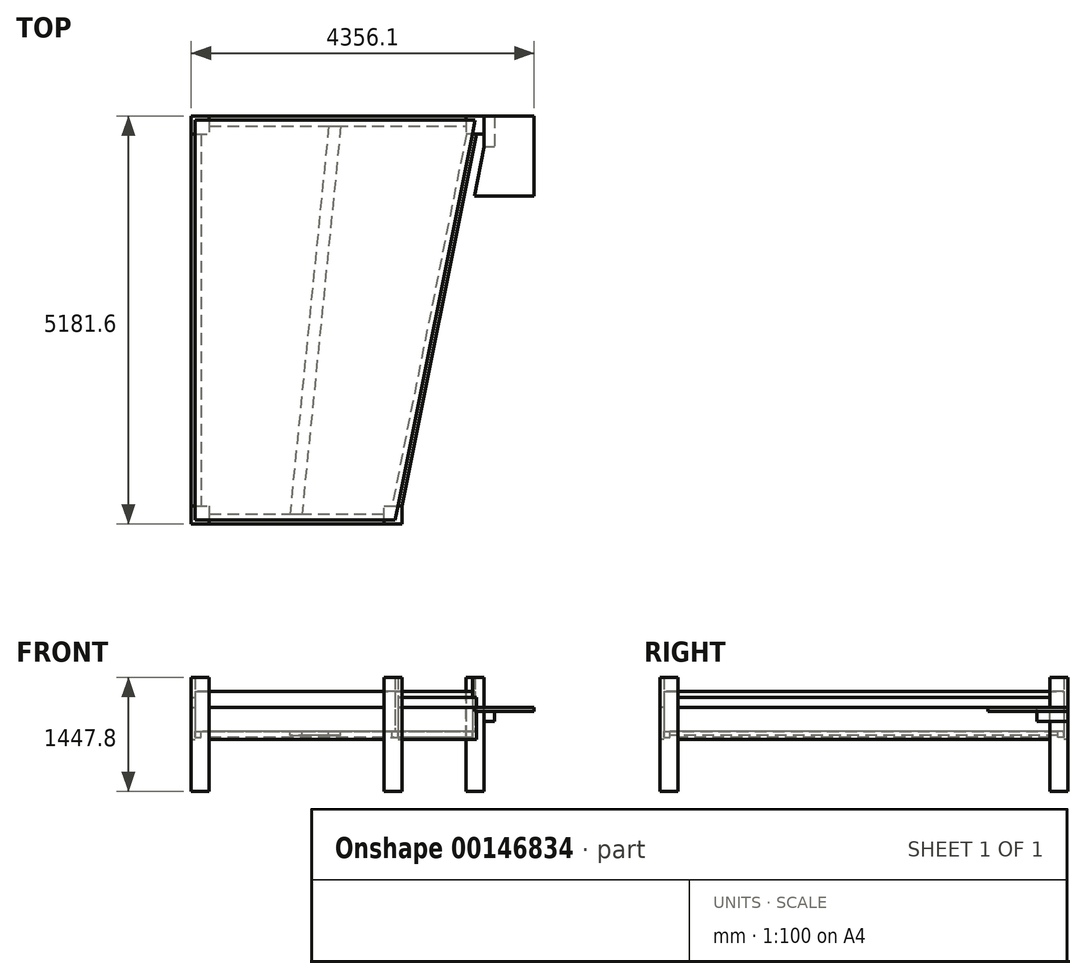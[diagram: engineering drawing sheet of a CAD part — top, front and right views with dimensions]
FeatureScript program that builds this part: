
annotation { "Feature Type Name" : "Feature", "Feature Type Description" : "" }
export const myFeature = defineFeature(function(context is Context, id is Id, definition is map)
    precondition{}
    {
        {
            var Q0;
            Q0=qCreatedBy(makeId("Top.planeOp"),FACE);
            var sketch = newSketch(context, id + "F0", { "sketchPlane" : qUnion([Q0])});
            skLineSegment(sketch, "E0", {"start": v(0, 0) * mm, "end": v(0, 5080) * mm});
            skLineSegment(sketch, "E1", {"start": v(0, 5080) * mm, "end": v(3556, 5080) * mm});
            skLineSegment(sketch, "E2", {"start": v(3556, 5080) * mm, "end": v(2540, 0) * mm});
            skPoint(sketch, "E2.endSnap0", {"position": v(1778, 5080) * mm});
            skLineSegment(sketch, "E3", {"start": v(2540, 0) * mm, "end": v(0, 0) * mm});
            skLineSegment(sketch, "E4.bottom", {"start": v(-50.8, 5130.8) * mm, "end": v(177.8, 5130.8) * mm});
            skLineSegment(sketch, "E4.top", {"start": v(-50.8, 4902.2) * mm, "end": v(177.8, 4902.2) * mm});
            skLineSegment(sketch, "E4.left", {"start": v(-50.8, 5130.8) * mm, "end": v(-50.8, 4902.2) * mm});
            skLineSegment(sketch, "E4.right", {"start": v(177.8, 5130.8) * mm, "end": v(177.8, 4902.2) * mm});
            skPoint(sketch, "E4.middle", {"position": v(0, 5080) * mm});
            skLineSegment(sketch, "E5.bottom", {"start": v(3670.3, 5130.8) * mm, "end": v(3441.7, 5130.8) * mm});
            skLineSegment(sketch, "E5.top", {"start": v(3670.3, 4902.2) * mm, "end": v(3441.7, 4902.2) * mm});
            skLineSegment(sketch, "E5.left", {"start": v(3670.3, 5130.8) * mm, "end": v(3670.3, 4902.2) * mm});
            skLineSegment(sketch, "E5.right", {"start": v(3441.7, 5130.8) * mm, "end": v(3441.7, 4902.2) * mm});
            skPoint(sketch, "E5.middle", {"position": v(3556, 5080) * mm});
            skLineSegment(sketch, "E6", {"start": v(177.8, 5130.8) * mm, "end": v(3441.7, 5130.8) * mm});
            skLineSegment(sketch, "E7.bottom", {"start": v(2398.77, -50.8) * mm, "end": v(2627.37, -50.8) * mm});
            skLineSegment(sketch, "E7.top", {"start": v(2398.77, 177.8) * mm, "end": v(2627.37, 177.8) * mm});
            skLineSegment(sketch, "E7.left", {"start": v(2398.77, -50.8) * mm, "end": v(2398.77, 177.8) * mm});
            skLineSegment(sketch, "E7.right", {"start": v(2627.37, -50.8) * mm, "end": v(2627.37, 177.8) * mm});
            skLineSegment(sketch, "E8", {"start": v(2627.37, 177.8) * mm, "end": v(3572.25, 4902.2) * mm});
            skLineSegment(sketch, "E9.bottom", {"start": v(-50.8, 177.8) * mm, "end": v(177.8, 177.8) * mm});
            skLineSegment(sketch, "E9.top", {"start": v(-50.8, -50.8) * mm, "end": v(177.8, -50.8) * mm});
            skLineSegment(sketch, "E9.left", {"start": v(-50.8, 177.8) * mm, "end": v(-50.8, -50.8) * mm});
            skLineSegment(sketch, "E9.right", {"start": v(177.8, 177.8) * mm, "end": v(177.8, -50.8) * mm});
            skLineSegment(sketch, "E10", {"start": v(177.8, -50.8) * mm, "end": v(2398.77, -50.8) * mm});
            skLineSegment(sketch, "E11", {"start": v(-50.8, 4902.2) * mm, "end": v(-50.8, 177.8) * mm});
            skLineSegment(sketch, "E12", {"start": v(76.2, 4902.2) * mm, "end": v(76.2, 177.8) * mm});
            skLineSegment(sketch, "E13", {"start": v(177.8, 76.2) * mm, "end": v(2398.77, 76.2) * mm});
            skLineSegment(sketch, "E14", {"start": v(177.8, 5003.8) * mm, "end": v(3441.7, 5003.8) * mm});
            skLineSegment(sketch, "E15", {"start": v(3442.73, 4902.2) * mm, "end": v(2497.85, 177.8) * mm});
            skLineSegment(sketch, "E16", {"start": v(1270, 0) * mm, "end": v(1778, 5080) * mm, "construction": true});
            skLineSegment(sketch, "E17", {"start": v(1854.58, 5080) * mm, "end": v(1346.58, 0) * mm});
            skLineSegment(sketch, "E18.MirrorCS", {"start": v(1701.42, 5080) * mm, "end": v(1193.42, 0) * mm});
            skSolve(sketch);
        }
        {
            var Q0;
            {var subQ6=sQuery(id+"F0.wireOp",EDGE,"E7.bottom");Q0=makeQuery(id+"F0.imprint","IMPRINT",FACE,{"disambiguationData":[TD([[makeQuery(id+"F0.imprint","IMPRINT",EDGE,{"derivedFrom":subQ6}),1.0]])]});}
            var Q1;
            {var subQ0=sQuery(id+"F0.wireOp",EDGE,"E3");var subQ1=sQuery(id+"F0.wireOp",EDGE,"E2");var subQ2=makeQuery(id+"F0.imprint","INTERSECT",VERTEX,{"derivedFrom":[subQ1,subQ0]});Q1=makeQuery(id+"F0.imprint","IMPRINT",FACE,{"disambiguationData":[TD([[makeQuery(id+"F0.imprint","IMPRINT",EDGE,{"disambiguationData":[TD([[subQ2,1.0]])],"derivedFrom":subQ1}),-1.0]])]});}
            var Q2;
            {var subQ0=sQuery(id+"F0.wireOp",EDGE,"E5.bottom");Q2=makeQuery(id+"F0.imprint","IMPRINT",FACE,{"disambiguationData":[TD([[makeQuery(id+"F0.imprint","IMPRINT",EDGE,{"derivedFrom":subQ0}),1.0]])]});}
            var Q3;
            {var subQ0=sQuery(id+"F0.wireOp",EDGE,"E2");var subQ1=sQuery(id+"F0.wireOp",EDGE,"E1");var subQ2=makeQuery(id+"F0.imprint","INTERSECT",VERTEX,{"derivedFrom":[subQ1,subQ0]});Q3=makeQuery(id+"F0.imprint","IMPRINT",FACE,{"disambiguationData":[TD([[makeQuery(id+"F0.imprint","IMPRINT",EDGE,{"disambiguationData":[TD([[subQ2,1.0]])],"derivedFrom":subQ1}),-1.0]])]});}
            var Q4;
            {var subQ0=sQuery(id+"F0.wireOp",EDGE,"E9.top");Q4=makeQuery(id+"F0.imprint","IMPRINT",FACE,{"disambiguationData":[TD([[makeQuery(id+"F0.imprint","IMPRINT",EDGE,{"derivedFrom":subQ0}),1.0]])]});}
            var Q5;
            {var subQ0=sQuery(id+"F0.wireOp",EDGE,"E3");var subQ1=sQuery(id+"F0.wireOp",EDGE,"E0");var subQ2=makeQuery(id+"F0.imprint","INTERSECT",VERTEX,{"derivedFrom":[subQ1,subQ0]});Q5=makeQuery(id+"F0.imprint","IMPRINT",FACE,{"disambiguationData":[TD([[makeQuery(id+"F0.imprint","IMPRINT",EDGE,{"disambiguationData":[TD([[subQ2,-1.0]])],"derivedFrom":subQ1}),-1.0]])]});}
            var Q6;
            {var subQ0=sQuery(id+"F0.wireOp",EDGE,"E1");var subQ1=sQuery(id+"F0.wireOp",EDGE,"E0");var subQ2=makeQuery(id+"F0.imprint","INTERSECT",VERTEX,{"derivedFrom":[subQ1,subQ0]});Q6=makeQuery(id+"F0.imprint","IMPRINT",FACE,{"disambiguationData":[TD([[makeQuery(id+"F0.imprint","IMPRINT",EDGE,{"disambiguationData":[TD([[subQ2,1.0]])],"derivedFrom":subQ1}),-1.0]])]});}
            var Q7;
            {var subQ4=sQuery(id+"F0.wireOp",EDGE,"E4.bottom");Q7=makeQuery(id+"F0.imprint","IMPRINT",FACE,{"disambiguationData":[TD([[makeQuery(id+"F0.imprint","IMPRINT",EDGE,{"derivedFrom":subQ4}),-1.0]])]});}
            extrude(context, id + "F1", {"entities" : qUnion([Q0, Q1, Q2, Q3, Q4, Q5, Q6, Q7]), "oppositeDirection" : true, "depth" : 762 * mm});
        }
        {
            var Q0;
            {var subQ0=sQuery(id+"F0.wireOp",EDGE,"E9.top");Q0=makeQuery(id+"F0.imprint","IMPRINT",FACE,{"disambiguationData":[TD([[makeQuery(id+"F0.imprint","IMPRINT",EDGE,{"derivedFrom":subQ0}),1.0]])]});}
            var Q1;
            {var subQ6=sQuery(id+"F0.wireOp",EDGE,"E7.bottom");Q1=makeQuery(id+"F0.imprint","IMPRINT",FACE,{"disambiguationData":[TD([[makeQuery(id+"F0.imprint","IMPRINT",EDGE,{"derivedFrom":subQ6}),1.0]])]});}
            var Q2;
            {var subQ0=sQuery(id+"F0.wireOp",EDGE,"E5.bottom");Q2=makeQuery(id+"F0.imprint","IMPRINT",FACE,{"disambiguationData":[TD([[makeQuery(id+"F0.imprint","IMPRINT",EDGE,{"derivedFrom":subQ0}),1.0]])]});}
            var Q3;
            {var subQ4=sQuery(id+"F0.wireOp",EDGE,"E4.bottom");Q3=makeQuery(id+"F0.imprint","IMPRINT",FACE,{"disambiguationData":[TD([[makeQuery(id+"F0.imprint","IMPRINT",EDGE,{"derivedFrom":subQ4}),-1.0]])]});}
            extrude(context, id + "F2", {"entities" : qUnion([Q0, Q1, Q2, Q3]), "operationType" : NewBodyOperationType.ADD, "depth" : 685.8 * mm});
        }
        {
            var Q0;
            {var subQ5=sQuery(id+"F0.wireOp",EDGE,"E11");Q0=makeQuery(id+"F0.imprint","IMPRINT",FACE,{"disambiguationData":[TD([[makeQuery(id+"F0.imprint","IMPRINT",EDGE,{"derivedFrom":subQ5}),1.0]])]});}
            var Q1;
            {var subQ5=sQuery(id+"F0.wireOp",EDGE,"E6");Q1=makeQuery(id+"F0.imprint","IMPRINT",FACE,{"disambiguationData":[TD([[makeQuery(id+"F0.imprint","IMPRINT",EDGE,{"derivedFrom":subQ5}),-1.0]])]});}
            var Q2;
            {var subQ4=sQuery(id+"F0.wireOp",EDGE,"E2");var subQ6=sQuery(id+"F0.wireOp",EDGE,"E5.top");var subQ8=makeQuery(id+"F0.imprint","INTERSECT",VERTEX,{"derivedFrom":[subQ4,subQ6]});Q2=makeQuery(id+"F0.imprint","IMPRINT",FACE,{"disambiguationData":[TD([[makeQuery(id+"F0.imprint","IMPRINT",EDGE,{"disambiguationData":[TD([[subQ8,-1.0]])],"derivedFrom":subQ4}),1.0]])]});}
            var Q3;
            {var subQ5=sQuery(id+"F0.wireOp",EDGE,"E10");Q3=makeQuery(id+"F0.imprint","IMPRINT",FACE,{"disambiguationData":[TD([[makeQuery(id+"F0.imprint","IMPRINT",EDGE,{"derivedFrom":subQ5}),1.0]])]});}
            extrude(context, id + "F3", {"entities" : qUnion([Q0, Q1, Q2, Q3]), "depth" : 304.8 * mm, "hasSecondDirection" : true, "secondDirectionOppositeDirection" : true, "secondDirectionDepth" : 101.6 * mm});
        }
        {
            var Q0;
            Q0=makeQuery(id+"F3.opExtrude","CAP_FACE",FACE,{"disambiguationData":[OSD([sQuery(id+"F0.wireOp",EDGE,"E2"),sQuery(id+"F0.wireOp",EDGE,"E5.top"),sQuery(id+"F0.wireOp",EDGE,"E7.top"),sQuery(id+"F0.wireOp",EDGE,"E8")])],"isStart":false});
            var sketch = newSketch(context, id + "F4", { "sketchPlane" : qUnion([Q0])});
            skLineSegment(sketch, "E19.0", {"start": v(3670.3, 4902.2) * mm, "end": v(3441.7, 4902.2) * mm});
            skLineSegment(sketch, "E19.1", {"start": v(3556, 5080) * mm, "end": v(2540, 0) * mm});
            skLineSegment(sketch, "E19.2", {"start": v(3670.3, 5130.8) * mm, "end": v(3441.7, 5130.8) * mm});
            skLineSegment(sketch, "E19.3", {"start": v(3441.7, 5130.8) * mm, "end": v(3441.7, 4902.2) * mm});
            skLineSegment(sketch, "E19.4", {"start": v(177.8, 5130.8) * mm, "end": v(3441.7, 5130.8) * mm});
            skLineSegment(sketch, "E19.6", {"start": v(3670.3, 5130.8) * mm, "end": v(3670.3, 4902.2) * mm});
            skLineSegment(sketch, "E19.7", {"start": v(0, 5080) * mm, "end": v(3556, 5080) * mm});
            skLineSegment(sketch, "E19.8", {"start": v(3670.3, 5130.8) * mm, "end": v(4305.3, 5130.8) * mm});
            skLineSegment(sketch, "E19.9", {"start": v(2627.37, 177.8) * mm, "end": v(3572.25, 4902.2) * mm});
            skLineSegment(sketch, "E19.11", {"start": v(3616.97, 4902.2) * mm, "end": v(3441.7, 4902.2) * mm});
            skLineSegment(sketch, "E19.12", {"start": v(3670.3, 5130.8) * mm, "end": v(3441.7, 5130.8) * mm});
            skLineSegment(sketch, "E19.13", {"start": v(3441.7, 5080) * mm, "end": v(3441.7, 4902.2) * mm});
            skLineSegment(sketch, "E19.14", {"start": v(3670.3, 5130.8) * mm, "end": v(3670.3, 4902.2) * mm});
            skLineSegment(sketch, "E19.15", {"start": v(3556, 5080) * mm, "end": v(3520.44, 4902.2) * mm});
            skLineSegment(sketch, "E19.16", {"start": v(3520.44, 4902.2) * mm, "end": v(2575.56, 177.8) * mm});
            skLineSegment(sketch, "E19.17", {"start": v(177.8, 5080) * mm, "end": v(3441.7, 5080) * mm});
            skLineSegment(sketch, "E19.18", {"start": v(177.8, 5130.8) * mm, "end": v(3441.7, 5130.8) * mm});
            skLineSegment(sketch, "E19.19", {"start": v(3441.7, 5130.8) * mm, "end": v(3441.7, 5080) * mm});
            skLineSegment(sketch, "E19.20", {"start": v(3670.3, 4902.2) * mm, "end": v(3441.7, 4902.2) * mm});
            skLineSegment(sketch, "E19.21", {"start": v(3441.7, 5130.8) * mm, "end": v(3441.7, 4902.2) * mm});
            skLineSegment(sketch, "E19.22", {"start": v(3441.7, 5080) * mm, "end": v(3556, 5080) * mm});
            skLineSegment(sketch, "E19.25", {"start": v(3670.3, 4902.2) * mm, "end": v(3520.44, 4902.2) * mm});
            skLineSegment(sketch, "E19.26", {"start": v(2627.37, 177.8) * mm, "end": v(3572.25, 4902.2) * mm});
            skLineSegment(sketch, "E19.27", {"start": v(3520.44, 4902.2) * mm, "end": v(2575.56, 177.8) * mm});
            skLineSegment(sketch, "E19.28", {"start": v(177.8, 5130.8) * mm, "end": v(3441.7, 5130.8) * mm});
            skLineSegment(sketch, "E19.29", {"start": v(177.8, 5080) * mm, "end": v(3441.7, 5080) * mm});
            skLineSegment(sketch, "E19.35", {"start": v(3670.3, 5130.8) * mm, "end": v(3441.7, 5130.8) * mm});
            skLineSegment(sketch, "E19.38", {"start": v(3670.3, 5130.8) * mm, "end": v(3670.3, 4902.2) * mm});
            skLineSegment(sketch, "E19.39", {"start": v(2627.37, 177.8) * mm, "end": v(3572.25, 4902.2) * mm});
            skLineSegment(sketch, "E19.42", {"start": v(3441.7, 5130.8) * mm, "end": v(3441.7, 5080) * mm});
            skLineSegment(sketch, "E19.45", {"start": v(3572.25, 4902.2) * mm, "end": v(3520.44, 4902.2) * mm});
            skLineSegment(sketch, "E19.46", {"start": v(3441.7, 5130.8) * mm, "end": v(3441.7, 5080) * mm});
            skLineSegment(sketch, "E19.47", {"start": v(3572.25, 4902.2) * mm, "end": v(3520.44, 4902.2) * mm});
            skLineSegment(sketch, "E20", {"start": v(4305.3, 5130.8) * mm, "end": v(4305.3, 4114.8) * mm});
            skLineSegment(sketch, "E21", {"start": v(4305.3, 4114.8) * mm, "end": v(3414.77, 4114.8) * mm});
            skLineSegment(sketch, "E22", {"start": v(3799.33, 5130.8) * mm, "end": v(3799.33, 4734.53) * mm});
            skLineSegment(sketch, "E23", {"start": v(3799.33, 4734.53) * mm, "end": v(3670.3, 4734.53) * mm});
            skLineSegment(sketch, "E24", {"start": v(3670.3, 4734.53) * mm, "end": v(3546.35, 4114.8) * mm});
            skLineSegment(sketch, "E25", {"start": v(3670.3, 4902.2) * mm, "end": v(3670.3, 4734.53) * mm});
            skSolve(sketch);
        }
        {
            var Q0;
            Q0=makeQuery(id+"F4.imprint","IMPRINT",FACE,{"disambiguationData":[TD([[makeQuery(id+"F4.imprint","IMPRINT",EDGE,{"derivedFrom":sQuery(id+"F4.wireOp",EDGE,"E19.8")}),-1.0]])]});
            var Q1;
            {var subQ2=sQuery(id+"F4.wireOp",EDGE,"E19.25");Q1=makeQuery(id+"F4.imprint","IMPRINT",FACE,{"disambiguationData":[TD([[makeQuery(id+"F4.imprint","IMPRINT",EDGE,{"derivedFrom":subQ2}),1.0]])]});}
            extrude(context, id + "F5", {"entities" : qUnion([Q0, Q1]), "oppositeDirection" : true, "depth" : 179.83 * mm});
        }
        {
            var Q0;
            {var subQ2=sQuery(id+"F4.wireOp",EDGE,"E20");Q0=makeQuery(id+"F4.imprint","IMPRINT",FACE,{"disambiguationData":[TD([[makeQuery(id+"F4.imprint","IMPRINT",EDGE,{"derivedFrom":subQ2}),-1.0]])]});}
            extrude(context, id + "F6", {"entities" : qUnion([Q0]), "operationType" : NewBodyOperationType.ADD, "oppositeDirection" : true, "depth" : 50.8 * mm});
        }
        {
            var Q0;
            {var subQ5=sQuery(id+"F0.wireOp",EDGE,"E12");Q0=makeQuery(id+"F0.imprint","IMPRINT",FACE,{"disambiguationData":[TD([[makeQuery(id+"F0.imprint","IMPRINT",EDGE,{"derivedFrom":subQ5}),-1.0]])]});}
            var Q1;
            {var subQ5=sQuery(id+"F0.wireOp",EDGE,"E14");Q1=makeQuery(id+"F0.imprint","IMPRINT",FACE,{"disambiguationData":[TD([[makeQuery(id+"F0.imprint","IMPRINT",EDGE,{"derivedFrom":subQ5}),1.0]])]});}
            var Q2;
            {var subQ5=sQuery(id+"F0.wireOp",EDGE,"E15");Q2=makeQuery(id+"F0.imprint","IMPRINT",FACE,{"disambiguationData":[TD([[makeQuery(id+"F0.imprint","IMPRINT",EDGE,{"derivedFrom":subQ5}),1.0]])]});}
            var Q3;
            {var subQ5=sQuery(id+"F0.wireOp",EDGE,"E13");Q3=makeQuery(id+"F0.imprint","IMPRINT",FACE,{"disambiguationData":[TD([[makeQuery(id+"F0.imprint","IMPRINT",EDGE,{"derivedFrom":subQ5}),-1.0]])]});}
            extrude(context, id + "F7", {"entities" : qUnion([Q0, Q1, Q2, Q3]), "oppositeDirection" : true, "depth" : 76.2 * mm});
        }
        {
            var Q0;
            {var subQ5=sQuery(id+"F0.wireOp",EDGE,"E12");Q0=makeQuery(id+"F0.imprint","IMPRINT",FACE,{"disambiguationData":[TD([[makeQuery(id+"F0.imprint","IMPRINT",EDGE,{"derivedFrom":subQ5}),-1.0]])]});}
            var Q1;
            {var subQ4=sQuery(id+"F0.wireOp",EDGE,"E0");var subQ7=sQuery(id+"F0.wireOp",EDGE,"E1");var subQ9=makeQuery(id+"F0.imprint","INTERSECT",VERTEX,{"derivedFrom":[subQ4,subQ7]});Q1=makeQuery(id+"F0.imprint","IMPRINT",FACE,{"disambiguationData":[TD([[makeQuery(id+"F0.imprint","IMPRINT",EDGE,{"disambiguationData":[TD([[subQ9,1.0]])],"derivedFrom":subQ4}),-1.0]])]});}
            var Q2;
            {var subQ5=sQuery(id+"F0.wireOp",EDGE,"E14");Q2=makeQuery(id+"F0.imprint","IMPRINT",FACE,{"disambiguationData":[TD([[makeQuery(id+"F0.imprint","IMPRINT",EDGE,{"derivedFrom":subQ5}),1.0]])]});}
            var Q3;
            {var subQ3=sQuery(id+"F0.wireOp",EDGE,"E12");Q3=makeQuery(id+"F0.imprint","IMPRINT",FACE,{"disambiguationData":[TD([[makeQuery(id+"F0.imprint","IMPRINT",EDGE,{"derivedFrom":subQ3}),1.0]])]});}
            var Q4;
            {var subQ5=sQuery(id+"F0.wireOp",EDGE,"E15");Q4=makeQuery(id+"F0.imprint","IMPRINT",FACE,{"disambiguationData":[TD([[makeQuery(id+"F0.imprint","IMPRINT",EDGE,{"derivedFrom":subQ5}),1.0]])]});}
            var Q5;
            {var subQ2=sQuery(id+"F0.wireOp",EDGE,"E2");var subQ4=sQuery(id+"F0.wireOp",EDGE,"E3");var subQ5=makeQuery(id+"F0.imprint","INTERSECT",VERTEX,{"derivedFrom":[subQ2,subQ4]});Q5=makeQuery(id+"F0.imprint","IMPRINT",FACE,{"disambiguationData":[TD([[makeQuery(id+"F0.imprint","IMPRINT",EDGE,{"disambiguationData":[TD([[subQ5,1.0]])],"derivedFrom":subQ2}),-1.0]])]});}
            var Q6;
            {var subQ5=sQuery(id+"F0.wireOp",EDGE,"E13");Q6=makeQuery(id+"F0.imprint","IMPRINT",FACE,{"disambiguationData":[TD([[makeQuery(id+"F0.imprint","IMPRINT",EDGE,{"derivedFrom":subQ5}),-1.0]])]});}
            var Q7;
            {var subQ4=sQuery(id+"F0.wireOp",EDGE,"E0");var subQ6=sQuery(id+"F0.wireOp",EDGE,"E3");var subQ7=makeQuery(id+"F0.imprint","INTERSECT",VERTEX,{"derivedFrom":[subQ4,subQ6]});Q7=makeQuery(id+"F0.imprint","IMPRINT",FACE,{"disambiguationData":[TD([[makeQuery(id+"F0.imprint","IMPRINT",EDGE,{"disambiguationData":[TD([[subQ7,-1.0]])],"derivedFrom":subQ4}),-1.0]])]});}
            var Q8;
            {var subQ4=sQuery(id+"F0.wireOp",EDGE,"E2");var subQ5=sQuery(id+"F0.wireOp",EDGE,"E1");var subQ6=makeQuery(id+"F0.imprint","INTERSECT",VERTEX,{"derivedFrom":[subQ5,subQ4]});Q8=makeQuery(id+"F0.imprint","IMPRINT",FACE,{"disambiguationData":[TD([[makeQuery(id+"F0.imprint","IMPRINT",EDGE,{"disambiguationData":[TD([[subQ6,1.0]])],"derivedFrom":subQ5}),-1.0]])]});}
            var Q9;
            {var subQ0=sQuery(id+"F0.wireOp",EDGE,"E18.MirrorCS");var subQ1=sQuery(id+"F0.wireOp",EDGE,"E13");var subQ2=makeQuery(id+"F0.imprint","INTERSECT",VERTEX,{"derivedFrom":[subQ1,subQ0]});Q9=makeQuery(id+"F0.imprint","IMPRINT",FACE,{"disambiguationData":[TD([[makeQuery(id+"F0.imprint","IMPRINT",EDGE,{"disambiguationData":[TD([[subQ2,-1.0]])],"derivedFrom":subQ1}),1.0]])]});}
            var Q10;
            {var subQ5=sQuery(id+"F0.wireOp",EDGE,"E15");Q10=makeQuery(id+"F0.imprint","IMPRINT",FACE,{"disambiguationData":[TD([[makeQuery(id+"F0.imprint","IMPRINT",EDGE,{"derivedFrom":subQ5}),-1.0]])]});}
            extrude(context, id + "F8", {"entities" : qUnion([Q0, Q1, Q2, Q3, Q4, Q5, Q6, Q7, Q8, Q9, Q10]), "depth" : 508 * mm});
        }
        {
            var Q0;
            Q0=makeQuery(id+"F3.opExtrude","CAP_FACE",FACE,{"disambiguationData":[OSD([sQuery(id+"F0.wireOp",EDGE,"E2"),sQuery(id+"F0.wireOp",EDGE,"E5.top"),sQuery(id+"F0.wireOp",EDGE,"E7.top"),sQuery(id+"F0.wireOp",EDGE,"E8")])],"isStart":false});
            var Q1;
            Q1=makeQuery(id+"F3.opExtrude","CAP_FACE",FACE,{"disambiguationData":[OSD([sQuery(id+"F0.wireOp",EDGE,"E0"),sQuery(id+"F0.wireOp",EDGE,"E4.top"),sQuery(id+"F0.wireOp",EDGE,"E9.bottom"),sQuery(id+"F0.wireOp",EDGE,"E11")])],"isStart":false});
            extrude(context, id + "F9", {"entities" : qUnion([Q0, Q1]), "depth" : 127 * mm});
        }
        {
            var Q0;
            {var subQ0=sQuery(id+"F0.wireOp",EDGE,"E18.MirrorCS");var subQ1=sQuery(id+"F0.wireOp",EDGE,"E13");var subQ2=makeQuery(id+"F0.imprint","INTERSECT",VERTEX,{"derivedFrom":[subQ1,subQ0]});Q0=makeQuery(id+"F0.imprint","IMPRINT",FACE,{"disambiguationData":[TD([[makeQuery(id+"F0.imprint","IMPRINT",EDGE,{"disambiguationData":[TD([[subQ2,-1.0]])],"derivedFrom":subQ1}),1.0]])]});}
            extrude(context, id + "F10", {"entities" : qUnion([Q0]), "oppositeDirection" : true, "depth" : 50.8 * mm});
        }
    });
